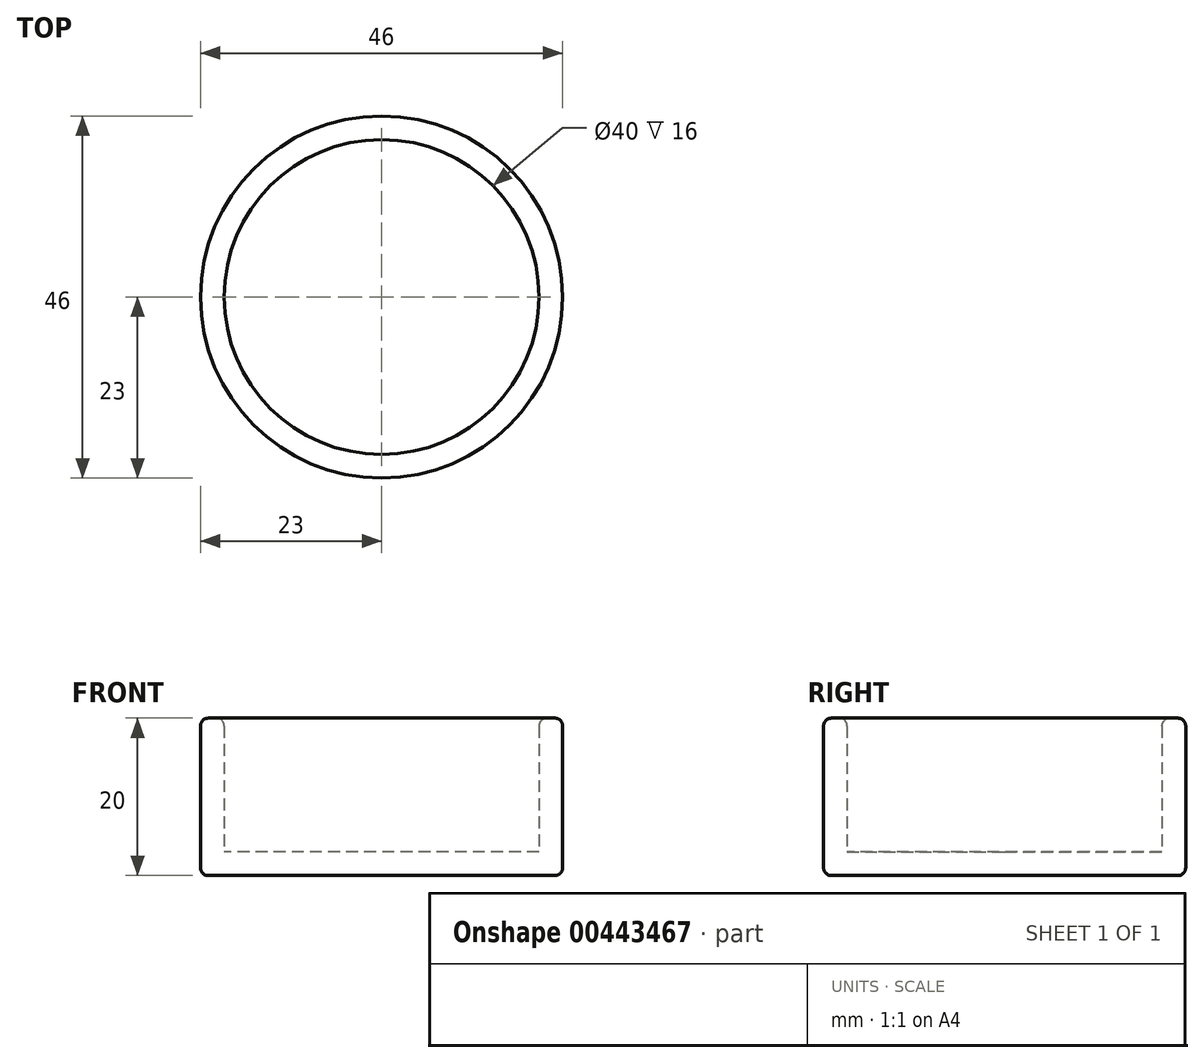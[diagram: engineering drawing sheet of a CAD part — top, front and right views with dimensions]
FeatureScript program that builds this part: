
annotation { "Feature Type Name" : "Feature", "Feature Type Description" : "" }
export const myFeature = defineFeature(function(context is Context, id is Id, definition is map)
    precondition{}
    {
        {
            var Q0;
            Q0=qCreatedBy(makeId("Top.planeOp"),FACE);
            var sketch = newSketch(context, id + "F0", { "sketchPlane" : qUnion([Q0])});
            skCircle(sketch, "E0", {"center": v(0, 0) * mm, "radius": 23 * mm});
            skCircle(sketch, "E1", {"center": v(0, 0) * mm, "radius": 20 * mm});
            skSolve(sketch);
        }
        {
            var Q0;
            Q0=makeQuery(id+"F0.imprint","IMPRINT",FACE,{"disambiguationData":[TD([[makeQuery(id+"F0.imprint","IMPRINT",EDGE,{"derivedFrom":sQuery(id+"F0.wireOp",EDGE,"E0")}),1.0]])]});
            extrude(context, id + "F1", {"entities" : qUnion([Q0]), "depth" : 20 * mm});
        }
        {
            var Q0;
            Q0=qCreatedBy(makeId("Top.planeOp"),FACE);
            var sketch = newSketch(context, id + "F2", { "sketchPlane" : qUnion([Q0])});
            skCircle(sketch, "E2", {"center": v(0, 0) * mm, "radius": 23 * mm});
            skSolve(sketch);
        }
        {
            var Q0;
            Q0=makeQuery(id+"F2.imprint","IMPRINT",FACE,{"disambiguationData":[TD([[makeQuery(id+"F2.imprint","IMPRINT",EDGE,{"derivedFrom":sQuery(id+"F2.wireOp",EDGE,"E2")}),1.0]])]});
            extrude(context, id + "F3", {"entities" : qUnion([Q0]), "operationType" : NewBodyOperationType.ADD, "depth" : 3 * mm});
        }
        {
            var Q0;
            Q0=makeQuery(id+"F1.opExtrude","CAP_EDGE",EDGE,{"disambiguationData":[OSD([sQuery(id+"F0.wireOp",EDGE,"E0")])],"isStart":false});
            var Q1;
            Q1=makeQuery(id+"F1.opExtrude","CAP_EDGE",EDGE,{"disambiguationData":[OSD([sQuery(id+"F0.wireOp",EDGE,"E0")])],"isStart":true});
            var Q2;
            Q2=makeQuery(id+"F1.opExtrude","CAP_EDGE",EDGE,{"disambiguationData":[OSD([sQuery(id+"F0.wireOp",EDGE,"E1")])],"isStart":false});
            fillet(context, id + "F4", {"entities" : qUnion([Q0, Q1, Q2]), "radius" : 1 * mm, "tangentPropagation" : true, "allowEdgeOverflow" : false});
        }
    });
